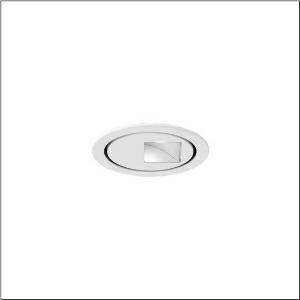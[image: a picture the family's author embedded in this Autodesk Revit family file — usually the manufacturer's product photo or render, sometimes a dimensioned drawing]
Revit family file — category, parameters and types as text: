
# Revit family: lunis_11_micro_round_51dj11cd1wf21
name_source: partatom
category: Lighting Fixtures
units: mm (PartAtom-declared; Revit-internal decimal feet)

## family parameters
Cut with Voids When Loaded = No
Host = Face
Light Source = No
Part Type = Normal
Room Calculation Point = No
Round Connector Dimension = Use Diameter
Shared = No

## types (1)
- Lunis 11 micro round (1 x LED 3000K / CRI = 80 (unbekannt), 1320 lm, 3000K)
    Apparent Load = 20 VA
    CIE Flux Codes = 42 75 96 100 100
    Color Rendering = 80
    Color Temperature = 3000K
    Default Elevation = 1800 mm
    Description = Lunis 11 micro round, downlight, light control with wallwasher, of highly reflective aluminium, highly specular, light emission: direct distribution, LED rated luminous flux: 1.320lm, light colour: 830, with terminal, 5-pole, mains connection: 220..230V, AC, 50/60Hz, LED module, of aluminium, highly specular, white, diameter: 114mm, clamping range: 1..40mm, recessing ring, of plastic, traffic white (RAL 9016), protection rating (complete): IP20, insulation class (complete): insulation class II (safety insulation), certification: CE, permissible ambient temperature for indoor applications: 0..+35°C, packaging unit: 1 piece
    Height = 0 mm  [stored 0 ft]
    Lamp = 1 x LED 3000K / CRI >= 80 (unbekannt)
    Lamp Light Flux = 1320 lm
    Lamp count = 1
    Length = 114 mm
    Luminous efficacy = 67 lm/W
    Manufacturer = Siteco
    ModVariant = No
    Model = 51DJ11CD1WF21
    Mounting Place = Ceiling
    Mounting Type = Recessed
    Number of Poles = 1
    OnlyDefault = Yes
    Power Factor = 1
    Product Name = Lunis 11 micro round
    Product group = downlight
    ProductGroupID = 400
    Protection Class = Protection class II
    Protection Degree = IP 20
    RLX_Detail_Level = 1
    RLX_Emergency_Light_Flux = 0 lm
    RLX_Emergency_Type = 0
    RLX_Emergency_Type_DB = No
    RlxData = <blob elided: 40401 chars, md5=06bd89e2>
    Socket = socket
    Standby Power = 0 W
    System Light Flux = 1320 lm
    System Power = 20 W
    Type Comments = Product without accessories
    Type Image = l_1004773.jpg
    URL = http://relux.com
    VarID = ---
    Voltage = 0 V
    Weight = 0.00 kg
    Width = 114 mm

note: [stored X ft] marks values corroborated as IEEE doubles in the binary element streams (Revit-internal decimal feet)

## geometry (parser evidence)
native form markers: Blend x4, Sweep x10
no freeform markers — native parametric forms only
